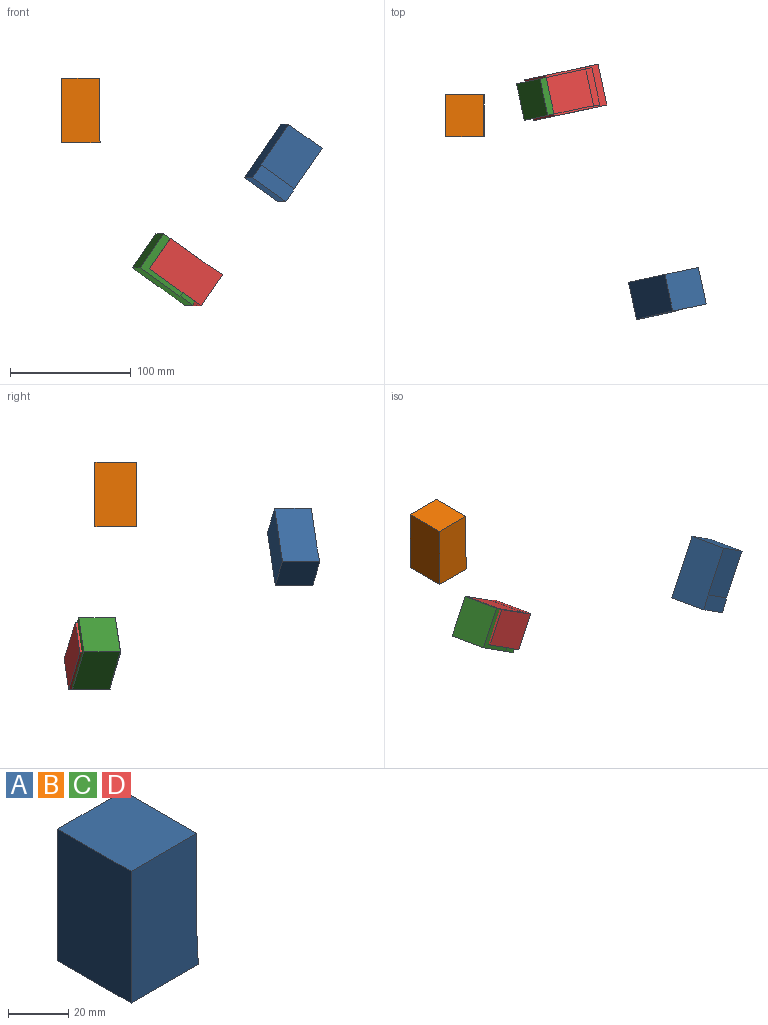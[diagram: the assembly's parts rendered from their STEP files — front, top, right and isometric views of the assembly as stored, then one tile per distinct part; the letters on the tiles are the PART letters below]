
ASSEMBLY  parts=4 mates=1
PART A: 7 faces, bbox 31.6x34.5x53.6 mm
  f0: plane 34.49x12.7mm, normal (1,0,0.05), area 438.7mm2, adj f1,f3,f4,f5
  f1: plane 53.59x31.62mm, normal (0,1,0), area 1663.2mm2, adj f0,f2,f4,f5,f6
  f2: plane 53.59x34.49mm, normal (-1,0,0), area 1848.6mm2, adj f1,f3,f4,f6
  f3: plane 53.59x31.62mm, normal (0,-1,0), area 1663.2mm2, adj f0,f2,f4,f5,f6
  f4: plane 34.49x31.62mm, normal (0,0,-1), area 1090.7mm2, adj f0,f1,f2,f3
  f5: plane 40.89x34.49mm, normal (1,0,0), area 1410.5mm2, adj f0,f1,f3,f6
  f6: plane 34.49x30.96mm, normal (0,0,1), area 1067.7mm2, adj f1,f2,f3,f5
PART B: same geometry as A
PART C: same geometry as A
PART D: same geometry as A
PLACE A rot(axis=(-0.35,0.28,-0.89),84.3deg) t=(112.91,-240.68,-88.09)mm
PLACE B t=(-37.54,0.61,-21.55)mm
PLACE C rot(axis=(0.5,-0.4,-0.77),92.8deg) t=(47.37,-70.58,-101.57)mm
PLACE D rot(axis=(0.1,-0.97,0.2),56.2deg) t=(34.3,29.74,-100.97)mm
MATE fastened D.f5 <-> C.f1  axis (0.56,0.12,0.82) through (-2.61,-27.99,-112.01)mm
